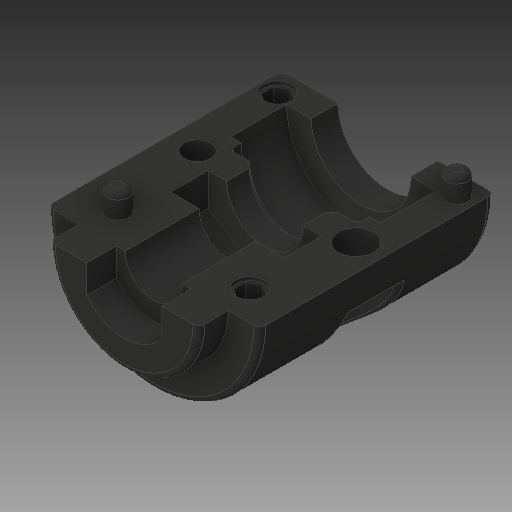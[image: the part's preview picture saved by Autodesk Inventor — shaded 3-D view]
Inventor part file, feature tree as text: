
AUTODESK INVENTOR PART (.ipt)
format: ipt  version: 2017 (Build 210142000, 142)  size: 282,624 bytes
history: native  units: in
note: dims shown in document units (in); Inventor stores cm internally (conversion verified against a paired STEP export)
features: fillet x1
ambient origin geometry x8: Origin, YZ Plane, XZ Plane, XY Plane, X Axis, Y Axis, Z Axis, Center Point
bodies: Solid1 (feature_tree)
feature tree (1):
  fillet  "Fillet1"  [1 undecoded]
note: 1 required parameter value undecoded (feature->parameter linkage not recoverable at this tier; creation-order binding heuristic only, values carry confidence <= 0.55)
